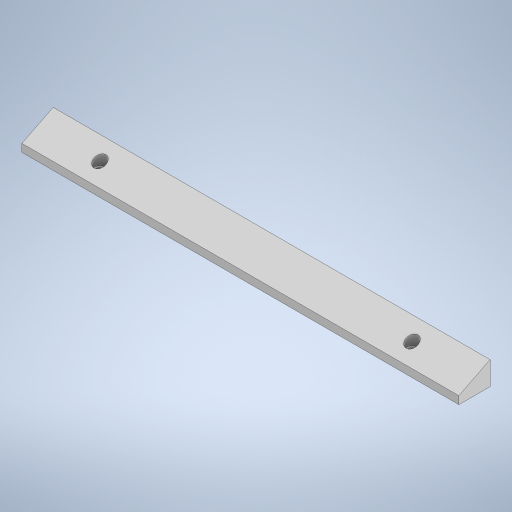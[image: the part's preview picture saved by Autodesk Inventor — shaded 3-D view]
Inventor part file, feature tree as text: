
AUTODESK INVENTOR PART (.ipt)
format: ipt  version: 2023 (Build 270158000, 158)  size: 270,336 bytes
history: native  units: in
note: dims shown in document units (in); Inventor stores cm internally (conversion verified against a paired STEP export)
features: sketch x6, extrude x5
ambient origin geometry x8: Origin, YZ Plane, XZ Plane, XY Plane, X Axis, Y Axis, Z Axis, Center Point
bodies: Solid1 (feature_tree)
feature tree (11):
  extrude  "Extrusion1"  Depth=0.3937in
  extrude  "Extrusion4"  Depth=0.1969in TaperAngle=0.0deg
  sketch  "Sketch7"  dims[d23=0.1772in d24=0.1772in]
  extrude  "Extrusion5"  Depth=0.1772in
  extrude  "Extrusion6"  Depth=0.2953in
  extrude  "Extrusion7"  Depth=0.3937in TaperAngle=0.0deg
  sketch  "Sketch1"  dims[d0=11.0236in d1=0.3937in]
  sketch  "Sketch6"  dims[d2=0.7874in d3=0.0in d21=0.1969in d22=0.0in]
  sketch  "Sketch8"  dims[d25=0.1181in d26=0.0in d27=0.2953in]
  sketch  "Sketch9"  dims[d28=0.2953in d29=0.3937in d30=0.0in]
  sketch  "Sketch10"  dims[d31=0.3937in d32=90.0deg d33=0.0in d34=0.0in d35=7.874in d36=0.3937in d37=0.3937in d38=1.5748in]
